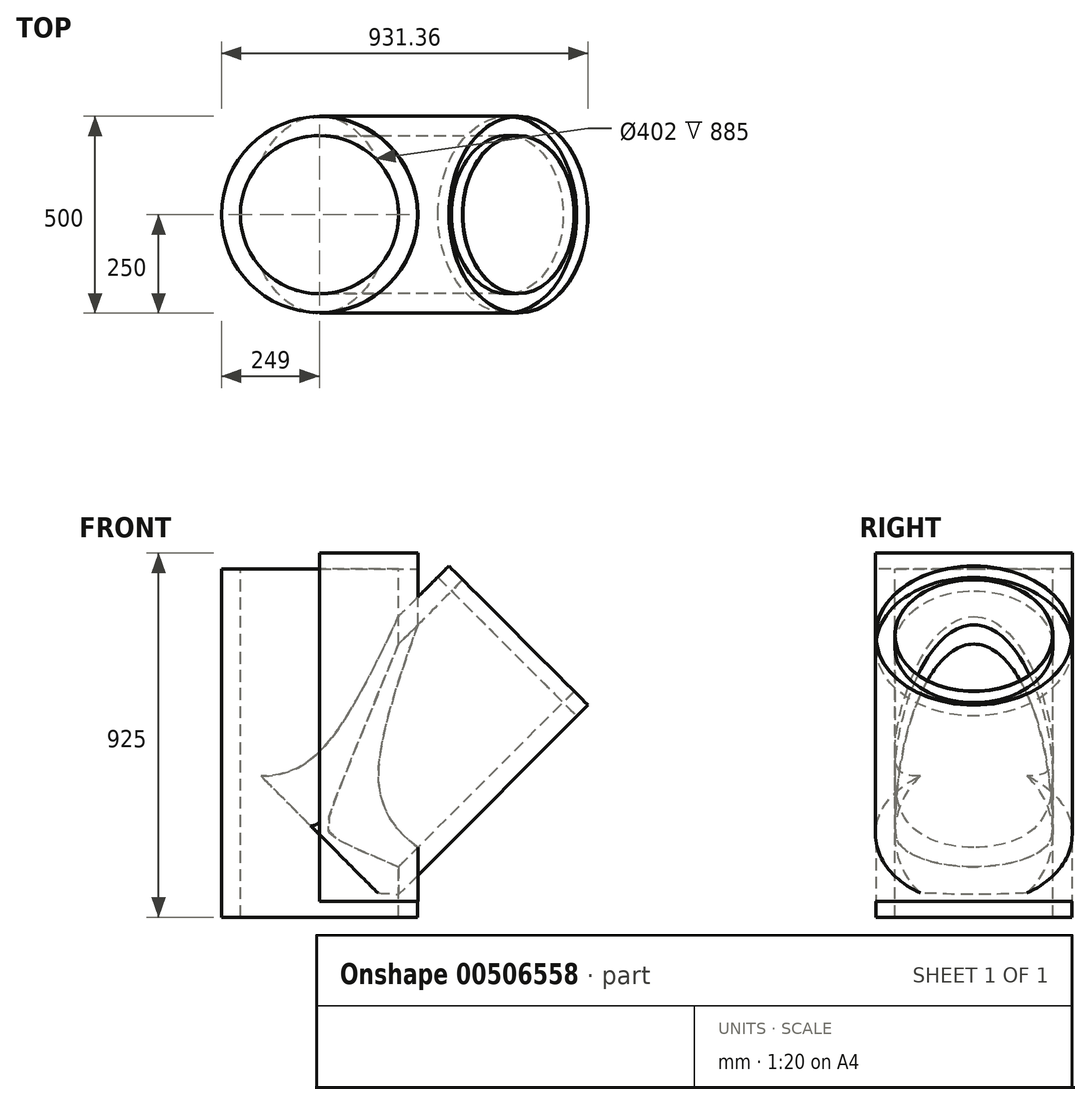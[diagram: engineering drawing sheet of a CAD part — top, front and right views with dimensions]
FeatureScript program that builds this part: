
annotation { "Feature Type Name" : "Feature", "Feature Type Description" : "" }
export const myFeature = defineFeature(function(context is Context, id is Id, definition is map)
    precondition{}
    {
        {
            var Q0;
            Q0=qCreatedBy(makeId("Front.planeOp"),FACE);
            var sketch = newSketch(context, id + "F0", { "sketchPlane" : qUnion([Q0])});
            skLineSegment(sketch, "E0", {"start": v(0, 377.94) * mm, "end": v(0, -525.84) * mm, "construction": true});
            skLineSegment(sketch, "E1", {"start": v(-250, -170) * mm, "end": v(-249, -170) * mm});
            skLineSegment(sketch, "E2", {"start": v(-249, -210) * mm, "end": v(-249, -170) * mm});
            skLineSegment(sketch, "E3", {"start": v(-249, -210) * mm, "end": v(-201, -210) * mm});
            skLineSegment(sketch, "E4", {"start": v(-201, -170) * mm, "end": v(-201, -210) * mm});
            skLineSegment(sketch, "E5", {"start": v(-201, -170) * mm, "end": v(-200, -170) * mm});
            skLineSegment(sketch, "E6", {"start": v(-722.24, 299.16) * mm, "end": v(793.2, -328.56) * mm, "construction": true});
            skLineSegment(sketch, "E7", {"start": v(0, 0) * mm, "end": v(-755.87, 0) * mm, "construction": true});
            skLineSegment(sketch, "E8", {"start": v(0, 0) * mm, "end": v(-598.81, 598.81) * mm, "construction": true});
            skLineSegment(sketch, "E9", {"start": v(-250, -170) * mm, "end": v(-250, 103.55) * mm});
            skLineSegment(sketch, "E10", {"start": v(-200, -170) * mm, "end": v(-200, 82.84) * mm});
            skLineSegment(sketch, "E11", {"start": v(328.8, 682.36) * mm, "end": v(329.51, 681.65) * mm});
            skLineSegment(sketch, "E12", {"start": v(301.23, 653.37) * mm, "end": v(329.51, 681.65) * mm});
            skLineSegment(sketch, "E13", {"start": v(301.23, 653.37) * mm, "end": v(335.17, 619.43) * mm});
            skLineSegment(sketch, "E14", {"start": v(363.45, 647.7) * mm, "end": v(335.17, 619.43) * mm});
            skLineSegment(sketch, "E15", {"start": v(363.45, 647.7) * mm, "end": v(364.16, 647) * mm});
            skLineSegment(sketch, "E16", {"start": v(364.16, 647) * mm, "end": v(-141.42, 141.42) * mm});
            skLineSegment(sketch, "E17", {"start": v(0, 0) * mm, "end": v(275.66, 275.66) * mm, "construction": true});
            skLineSegment(sketch, "E18", {"start": v(-200, 82.84) * mm, "end": v(-200, 715) * mm});
            skLineSegment(sketch, "E19", {"start": v(-200, 715) * mm, "end": v(-201, 715) * mm});
            skLineSegment(sketch, "E20", {"start": v(-201, 675) * mm, "end": v(-201, 715) * mm});
            skLineSegment(sketch, "E21", {"start": v(-201, 675) * mm, "end": v(-249, 675) * mm});
            skLineSegment(sketch, "E22", {"start": v(-249, 715) * mm, "end": v(-249, 675) * mm});
            skLineSegment(sketch, "E23", {"start": v(-249, 715) * mm, "end": v(-250, 715) * mm});
            skLineSegment(sketch, "E24", {"start": v(-250, 715) * mm, "end": v(-250, 103.55) * mm});
            skLineSegment(sketch, "E25.trimOffspring", {"start": v(-176.78, 176.78) * mm, "end": v(328.8, 682.36) * mm});
            skLineSegment(sketch, "E26", {"start": v(-176.78, 176.78) * mm, "end": v(-141.42, 141.42) * mm});
            skSolve(sketch);
        }
        {
            var Q0;
            Q0=makeQuery(id+"F0.imprint","IMPRINT",FACE,{"disambiguationData":[TD([[makeQuery(id+"F0.imprint","IMPRINT",EDGE,{"derivedFrom":sQuery(id+"F0.wireOp",EDGE,"E1")}),1.0]])]});
            var Q1;
            Q1=sQuery(id+"F0.wireOp",EDGE,"E0");
            revolve(context, id + "F1", {"entities" : qUnion([Q0]), "axis" : qUnion([Q1]), "revolveType" : RevolveType.FULL});
        }
        {
            var Q0;
            Q0=makeQuery(id+"F0.imprint","IMPRINT",FACE,{"disambiguationData":[TD([[makeQuery(id+"F0.imprint","IMPRINT",EDGE,{"derivedFrom":sQuery(id+"F0.wireOp",EDGE,"E11")}),-1.0]])]});
            var Q1;
            Q1=sQuery(id+"F0.wireOp",EDGE,"E17");
            revolve(context, id + "F2", {"entities" : qUnion([Q0]), "axis" : qUnion([Q1]), "revolveType" : RevolveType.FULL});
        }
        {
            var Q0;
            Q0=makeQuery(id+"F2.opRevolve","SWEPT_FACE",FACE,{"disambiguationData":[OSD([sQuery(id+"F0.wireOp",EDGE,"E13")])]});
            var sketch = newSketch(context, id + "F3", { "sketchPlane" : qUnion([Q0])});
            skCircle(sketch, "E27.0", {"center": v(0, 0) * mm, "radius": 200 * mm});
            skSolve(sketch);
        }
        {
            var Q0;
            Q0=qSketchRegion(id+"F3",true);
            var Q1;
            Q1=makeQuery(id+"F2.opRevolve","SWEPT_FACE",FACE,{"disambiguationData":[OSD([sQuery(id+"F0.wireOp",EDGE,"RudJvVgb-d4Mj-z1rT-Vhq7-xhC1Clk5OM9b")])]});
            extrude(context, id + "F4", {"entities" : qUnion([Q0]), "operationType" : NewBodyOperationType.REMOVE, "oppositeDirection" : true, "depth" : 675 * mm, "endBoundEntityFace" : qUnion([Q1]), "offsetDistance" : 25 * mm});
        }
        {
            var Q0;
            Q0=makeQuery(id+"F1.opRevolve","SWEPT_FACE",FACE,{"disambiguationData":[OSD([sQuery(id+"F0.wireOp",EDGE,"E3")])]});
            cPlane(context, id + "F5", {"entities" : qUnion([Q0]), "cplaneType" : CPlaneType.OFFSET, "offset" : 500 * mm, "width" : 150 * mm, "height" : 150 * mm});
        }
        {
            var Q0;
            Q0=qCreatedBy(id+"F5.planeOp",FACE);
            var sketch = newSketch(context, id + "F6", { "sketchPlane" : qUnion([Q0])});
            skCircle(sketch, "E28.0", {"center": v(0, 0) * mm, "radius": 201 * mm});
            skCircle(sketch, "E29.0", {"center": v(0, 0) * mm, "radius": 249 * mm, "construction": true});
            skArc(sketch, "E30", {"start": v(0, -249) * mm, "mid": v(-249, 0) * mm, "end": v(0, 249) * mm});
            skLineSegment(sketch, "E31", {"start": v(0, 249) * mm, "end": v(0, 672.32) * mm});
            skArc(sketch, "E32", {"start": v(0, 672.32) * mm, "mid": v(-672.32, 0) * mm, "end": v(0, -672.32) * mm});
            skLineSegment(sketch, "E33", {"start": v(0, -249) * mm, "end": v(0, -672.32) * mm});
            skSolve(sketch);
        }
        {
            var Q0;
            Q0=qSketchRegion(id+"F6",true);
            extrude(context, id + "F7", {"entities" : qUnion([Q0]), "operationType" : NewBodyOperationType.REMOVE, "oppositeDirection" : true, "depth" : 3000 * mm, "offsetDistance" : 25 * mm});
        }
    });
